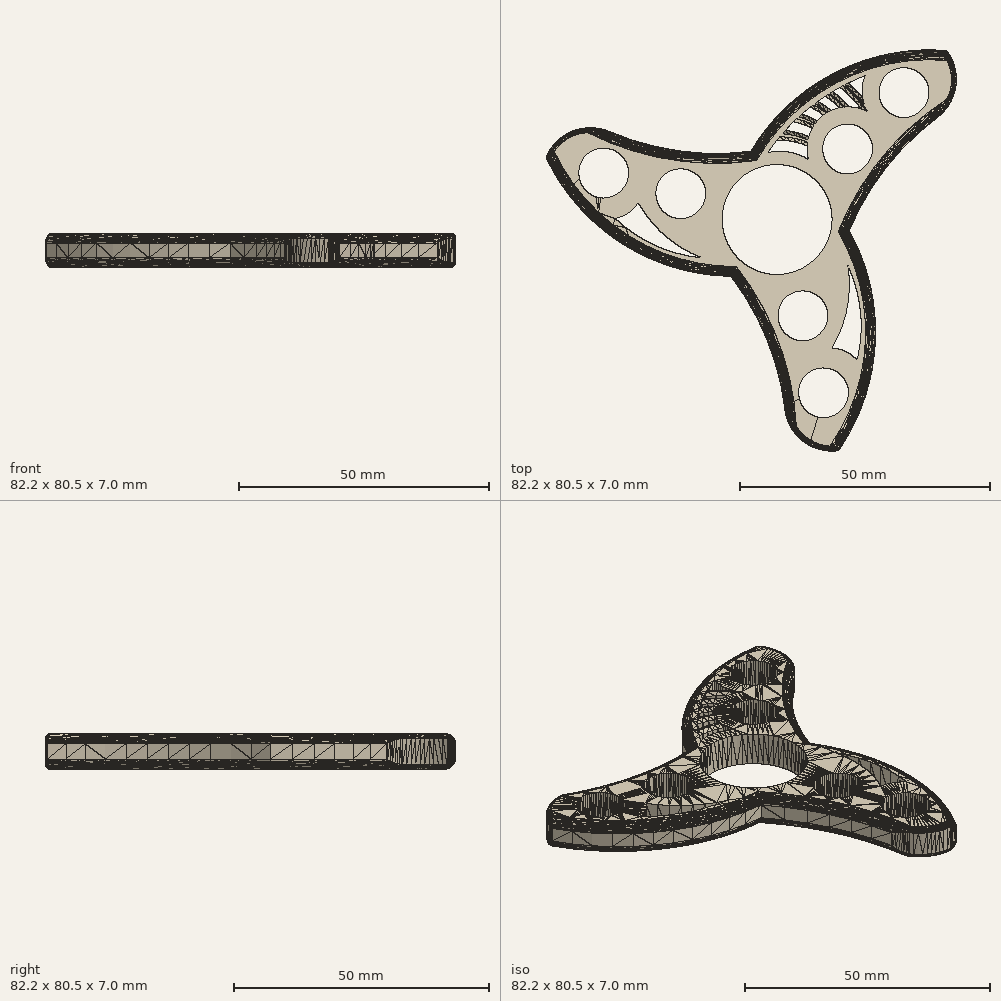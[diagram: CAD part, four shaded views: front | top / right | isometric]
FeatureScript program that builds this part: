
annotation { "Feature Type Name" : "Feature", "Feature Type Description" : "" }
export const myFeature = defineFeature(function(context is Context, id is Id, definition is map)
    precondition{}
    {
        {
            var Q0;
            Q0=qCreatedBy(makeId("Top.planeOp"),FACE);
            var sketch = newSketch(context, id + "F0", { "sketchPlane" : qUnion([Q0])});
            skCircle(sketch, "E0", {"center": v(0, 0) * mm, "radius": 11.03 * mm});
            skLineSegment(sketch, "E1", {"start": v(0, 0) * mm, "end": v(33.94, 33.94) * mm, "construction": true});
            skCircle(sketch, "E2", {"center": v(25.46, 25.46) * mm, "radius": 6.5 * mm, "construction": true});
            skCircle(sketch, "E3", {"center": v(14.14, 14.14) * mm, "radius": 6.5 * mm, "construction": true});
            skCircle(sketch, "E4", {"center": v(14.14, 14.14) * mm, "radius": 5 * mm});
            skCircle(sketch, "E5", {"center": v(25.46, 25.46) * mm, "radius": 5 * mm});
            skArc(sketch, "E6", {"start": v(33.94, 33.94) * mm, "mid": v(11.46, 29.38) * mm, "end": v(-5.27, 13.69) * mm});
            skArc(sketch, "E7", {"start": v(32.35, 20.51) * mm, "mid": v(21.9, 10.32) * mm, "end": v(14.49, -2.28) * mm});
            skArc(sketch, "E8", {"start": v(32.35, 20.51) * mm, "mid": v(35.92, 26.9) * mm, "end": v(33.94, 33.94) * mm});
            skArc(sketch, "E9.1.0", {"start": v(-33.94, 17.76) * mm, "mid": v(-41.25, 17.65) * mm, "end": v(-46.36, 12.42) * mm});
            skArc(sketch, "E9.1.1", {"start": v(-46.36, 12.42) * mm, "mid": v(-31.17, -4.76) * mm, "end": v(-9.22, -11.4) * mm});
            skArc(sketch, "E9.1.2", {"start": v(-32.47, 0.2) * mm, "mid": v(-29.84, 1.28) * mm, "end": v(-27.83, 3.32) * mm});
            skArc(sketch, "E9.1.3", {"start": v(-27.83, 3.32) * mm, "mid": v(-22.42, -3.3) * mm, "end": v(-15.06, -7.68) * mm});
            skArc(sketch, "E9.1.4", {"start": v(-32.47, 0.2) * mm, "mid": v(-24.43, -5.21) * mm, "end": v(-15.06, -7.68) * mm});
            skArc(sketch, "E9.1.5", {"start": v(-33.94, 17.76) * mm, "mid": v(-19.88, 13.8) * mm, "end": v(-5.27, 13.69) * mm});
            skCircle(sketch, "E9.1.6", {"center": v(-34.77, 9.32) * mm, "radius": 5 * mm});
            skCircle(sketch, "E9.1.7", {"center": v(-19.32, 5.18) * mm, "radius": 5 * mm});
            skCircle(sketch, "E9.1.8", {"center": v(-34.77, 9.32) * mm, "radius": 6.5 * mm, "construction": true});
            skCircle(sketch, "E9.1.9", {"center": v(-19.32, 5.18) * mm, "radius": 6.5 * mm, "construction": true});
            skArc(sketch, "E9.2.0", {"start": v(1.59, -38.28) * mm, "mid": v(5.34, -44.55) * mm, "end": v(12.42, -46.36) * mm});
            skArc(sketch, "E9.2.1", {"start": v(12.42, -46.36) * mm, "mid": v(19.7, -24.61) * mm, "end": v(14.49, -2.28) * mm});
            skArc(sketch, "E9.2.2", {"start": v(16.07, -28.22) * mm, "mid": v(13.8, -26.48) * mm, "end": v(11.04, -25.76) * mm});
            skArc(sketch, "E9.2.3", {"start": v(11.04, -25.76) * mm, "mid": v(14.07, -17.76) * mm, "end": v(14.18, -9.2) * mm});
            skArc(sketch, "E9.2.4", {"start": v(16.07, -28.22) * mm, "mid": v(16.73, -18.55) * mm, "end": v(14.18, -9.2) * mm});
            skArc(sketch, "E9.2.5", {"start": v(1.59, -38.28) * mm, "mid": v(-2.01, -24.12) * mm, "end": v(-9.22, -11.4) * mm});
            skCircle(sketch, "E9.2.6", {"center": v(9.32, -34.77) * mm, "radius": 5 * mm});
            skCircle(sketch, "E9.2.7", {"center": v(5.18, -19.32) * mm, "radius": 5 * mm});
            skCircle(sketch, "E9.2.8", {"center": v(9.32, -34.77) * mm, "radius": 6.5 * mm, "construction": true});
            skCircle(sketch, "E9.2.9", {"center": v(5.18, -19.32) * mm, "radius": 6.5 * mm, "construction": true});
            skPoint(sketch, "E10.orphan", {"position": v(-5.41, 13.45) * mm});
            skPoint(sketch, "E11.orphan", {"position": v(14.36, -2.04) * mm});
            skPoint(sketch, "E12.orphan", {"position": v(12.82, -6.77) * mm});
            skPoint(sketch, "E13.orphan", {"position": v(-12.27, -7.72) * mm});
            skPoint(sketch, "E14.orphan", {"position": v(-8.94, -11.41) * mm});
            skLineSegment(sketch, "E15", {"start": v(18.56, -32.6) * mm, "end": v(35.6, 25.32) * mm, "construction": true});
            skArc(sketch, "E16", {"start": v(17.66, 28.84) * mm, "mid": v(15.95, 28.13) * mm, "end": v(14.29, 27.35) * mm});
            skArc(sketch, "E17", {"start": v(6.3, 12.06) * mm, "mid": v(2.36, 13.55) * mm, "end": v(-1.83, 13.41) * mm});
            skArc(sketch, "E18", {"start": v(16.92, 22.19) * mm, "mid": v(15.73, 22.49) * mm, "end": v(14.51, 22.6) * mm});
            skArc(sketch, "E19", {"start": v(17.66, 28.84) * mm, "mid": v(17.1, 26.69) * mm, "end": v(17.14, 24.47) * mm});
            skArc(sketch, "E20.0.3.0", {"start": v(8.1, 19.77) * mm, "mid": v(6.61, 20.54) * mm, "end": v(5.06, 21.16) * mm});
            skLineSegment(sketch, "E20.direction1", {"start": v(0.3, 0.77) * mm, "end": v(25.3, 0.77) * mm, "construction": true});
            skLineSegment(sketch, "E20.direction2", {"start": v(0.3, 0.77) * mm, "end": v(0.3, 2.77) * mm, "construction": true});
            skArc(sketch, "E21", {"start": v(9.32, 20.93) * mm, "mid": v(8.06, 21.8) * mm, "end": v(6.7, 22.53) * mm});
            skArc(sketch, "E22", {"start": v(10.84, 21.84) * mm, "mid": v(9.57, 22.82) * mm, "end": v(8.22, 23.68) * mm});
            skArc(sketch, "E23", {"start": v(12.54, 22.42) * mm, "mid": v(11.18, 23.63) * mm, "end": v(9.72, 24.72) * mm});
            skPoint(sketch, "E23.startSnap0", {"position": v(13.15, 22.53) * mm});
            skArc(sketch, "E24", {"start": v(14.51, 22.6) * mm, "mid": v(12.93, 24.2) * mm, "end": v(11.2, 25.66) * mm});
            skArc(sketch, "E25", {"start": v(16.92, 22.19) * mm, "mid": v(14.9, 24.45) * mm, "end": v(12.67, 26.5) * mm});
            skArc(sketch, "E26", {"start": v(17.14, 24.47) * mm, "mid": v(15.76, 25.95) * mm, "end": v(14.29, 27.35) * mm});
            skArc(sketch, "E27.trimOffspring", {"start": v(-4.32, 15.2) * mm, "mid": v(-5.08, 14.93) * mm, "end": v(-5.82, 14.63) * mm});
            skArc(sketch, "E28.trimOffspring", {"start": v(6.05, 14.79) * mm, "mid": v(3.1, 15.66) * mm, "end": v(0.04, 15.92) * mm});
            skArc(sketch, "E29.trimOffspring", {"start": v(6.4, 16.64) * mm, "mid": v(4.1, 17.44) * mm, "end": v(1.7, 17.86) * mm});
            skArc(sketch, "E30.trimOffspring", {"start": v(7.1, 18.32) * mm, "mid": v(5.28, 19.08) * mm, "end": v(3.39, 19.6) * mm});
            skPoint(sketch, "E31.orphan", {"position": v(8.73, 19.36) * mm});
            skPoint(sketch, "E32.orphan", {"position": v(13.15, 21.8) * mm});
            skArc(sketch, "E33.trimOffspring", {"start": v(12.67, 26.5) * mm, "mid": v(11.94, 26.1) * mm, "end": v(11.2, 25.66) * mm});
            skArc(sketch, "E34.trimOffspring", {"start": v(9.72, 24.72) * mm, "mid": v(8.96, 24.21) * mm, "end": v(8.22, 23.68) * mm});
            skArc(sketch, "E35.trimOffspring", {"start": v(12.54, 22.42) * mm, "mid": v(11.68, 22.18) * mm, "end": v(10.84, 21.84) * mm});
            skArc(sketch, "E36.trimOffspring", {"start": v(6.7, 22.53) * mm, "mid": v(5.87, 21.85) * mm, "end": v(5.06, 21.16) * mm});
            skArc(sketch, "E37.trimOffspring", {"start": v(3.39, 19.6) * mm, "mid": v(2.53, 18.74) * mm, "end": v(1.7, 17.86) * mm});
            skArc(sketch, "E38.trimOffspring", {"start": v(7.1, 18.32) * mm, "mid": v(6.7, 17.5) * mm, "end": v(6.4, 16.64) * mm});
            skArc(sketch, "E39.trimOffspring", {"start": v(0.04, 15.92) * mm, "mid": v(-0.92, 14.68) * mm, "end": v(-1.83, 13.41) * mm});
            skArc(sketch, "E40.trimOffspring", {"start": v(6.05, 14.79) * mm, "mid": v(6.06, 13.41) * mm, "end": v(6.3, 12.06) * mm});
            skArc(sketch, "E41", {"start": v(9.32, 20.93) * mm, "mid": v(8.67, 20.4) * mm, "end": v(8.1, 19.77) * mm});
            skSolve(sketch);
        }
        {
            var Q0;
            Q0=makeQuery(id+"F0.imprint","IMPRINT",FACE,{"disambiguationData":[TD([[makeQuery(id+"F0.imprint","IMPRINT",EDGE,{"derivedFrom":sQuery(id+"F0.wireOp",EDGE,"E0")}),-1.0]])]});
            extrude(context, id + "F1", {"entities" : qUnion([Q0]), "depth" : 7 * mm});
        }
        {
            var Q0;
            Q0=makeQuery(id+"F1.opExtrude","CAP_EDGE",EDGE,{"disambiguationData":[OSD([sQuery(id+"F0.wireOp",EDGE,"E9.1.1")])],"isStart":false});
            var Q1;
            Q1=makeQuery(id+"F1.opExtrude","CAP_EDGE",EDGE,{"disambiguationData":[OSD([sQuery(id+"F0.wireOp",EDGE,"E9.2.5")])],"isStart":false});
            var Q2;
            Q2=makeQuery(id+"F1.opExtrude","CAP_EDGE",EDGE,{"disambiguationData":[OSD([sQuery(id+"F0.wireOp",EDGE,"E9.2.1")])],"isStart":false});
            var Q3;
            Q3=makeQuery(id+"F1.opExtrude","CAP_EDGE",EDGE,{"disambiguationData":[OSD([sQuery(id+"F0.wireOp",EDGE,"E7")])],"isStart":false});
            var Q4;
            Q4=makeQuery(id+"F1.opExtrude","CAP_EDGE",EDGE,{"disambiguationData":[OSD([sQuery(id+"F0.wireOp",EDGE,"E6")])],"isStart":false});
            var Q5;
            Q5=makeQuery(id+"F1.opExtrude","CAP_EDGE",EDGE,{"disambiguationData":[OSD([sQuery(id+"F0.wireOp",EDGE,"E9.1.5")])],"isStart":false});
            var Q6;
            Q6=makeQuery(id+"F1.opExtrude","CAP_EDGE",EDGE,{"disambiguationData":[OSD([sQuery(id+"F0.wireOp",EDGE,"E6")])],"isStart":true});
            var Q7;
            Q7=makeQuery(id+"F1.opExtrude","CAP_EDGE",EDGE,{"disambiguationData":[OSD([sQuery(id+"F0.wireOp",EDGE,"E9.1.5")])],"isStart":true});
            var Q8;
            Q8=makeQuery(id+"F1.opExtrude","CAP_EDGE",EDGE,{"disambiguationData":[OSD([sQuery(id+"F0.wireOp",EDGE,"E7")])],"isStart":true});
            var Q9;
            Q9=makeQuery(id+"F1.opExtrude","CAP_EDGE",EDGE,{"disambiguationData":[OSD([sQuery(id+"F0.wireOp",EDGE,"E9.2.1")])],"isStart":true});
            var Q10;
            Q10=makeQuery(id+"F1.opExtrude","CAP_EDGE",EDGE,{"disambiguationData":[OSD([sQuery(id+"F0.wireOp",EDGE,"E9.2.5")])],"isStart":true});
            var Q11;
            Q11=makeQuery(id+"F1.opExtrude","CAP_EDGE",EDGE,{"disambiguationData":[OSD([sQuery(id+"F0.wireOp",EDGE,"E9.1.1")])],"isStart":true});
            fillet(context, id + "F2", {"entities" : qUnion([Q0, Q1, Q2, Q3, Q4, Q5, Q6, Q7, Q8, Q9, Q10, Q11]), "radius" : 2 * mm, "tangentPropagation" : true, "allowEdgeOverflow" : false});
        }
        {
            var Q0;
            Q0=makeQuery(id+"F1.opExtrude","CAP_EDGE",EDGE,{"disambiguationData":[OSD([sQuery(id+"F0.wireOp",EDGE,"E9.1.0")])],"isStart":false});
            var Q1;
            Q1=makeQuery(id+"F1.opExtrude","CAP_EDGE",EDGE,{"disambiguationData":[OSD([sQuery(id+"F0.wireOp",EDGE,"E9.2.0")])],"isStart":false});
            var Q2;
            Q2=makeQuery(id+"F1.opExtrude","CAP_EDGE",EDGE,{"disambiguationData":[OSD([sQuery(id+"F0.wireOp",EDGE,"E8")])],"isStart":false});
            var Q3;
            Q3=makeQuery(id+"F1.opExtrude","CAP_EDGE",EDGE,{"disambiguationData":[OSD([sQuery(id+"F0.wireOp",EDGE,"E9.2.0")])],"isStart":true});
            var Q4;
            Q4=makeQuery(id+"F1.opExtrude","CAP_EDGE",EDGE,{"disambiguationData":[OSD([sQuery(id+"F0.wireOp",EDGE,"E9.1.0")])],"isStart":true});
            var Q5;
            Q5=makeQuery(id+"F1.opExtrude","CAP_EDGE",EDGE,{"disambiguationData":[OSD([sQuery(id+"F0.wireOp",EDGE,"E8")])],"isStart":true});
            fillet(context, id + "F3", {"entities" : qUnion([Q0, Q1, Q2, Q3, Q4, Q5]), "radius" : 1 * mm, "tangentPropagation" : true, "allowEdgeOverflow" : false});
        }
        {
            var Q0;
            Q0=makeQuery(id+"F1.opExtrude","CAP_EDGE",EDGE,{"disambiguationData":[OSD([sQuery(id+"F0.wireOp",EDGE,"E28.trimOffspring")])],"isStart":false});
            var Q1;
            Q1=makeQuery(id+"F1.opExtrude","CAP_EDGE",EDGE,{"disambiguationData":[OSD([sQuery(id+"F0.wireOp",EDGE,"E29.trimOffspring")])],"isStart":false});
            var Q2;
            Q2=makeQuery(id+"F1.opExtrude","CAP_EDGE",EDGE,{"disambiguationData":[OSD([sQuery(id+"F0.wireOp",EDGE,"E20.0.3.0")])],"isStart":false});
            var Q3;
            Q3=makeQuery(id+"F1.opExtrude","CAP_EDGE",EDGE,{"disambiguationData":[OSD([sQuery(id+"F0.wireOp",EDGE,"E21")])],"isStart":false});
            var Q4;
            Q4=makeQuery(id+"F1.opExtrude","CAP_EDGE",EDGE,{"disambiguationData":[OSD([sQuery(id+"F0.wireOp",EDGE,"E22")])],"isStart":false});
            var Q5;
            Q5=makeQuery(id+"F1.opExtrude","CAP_EDGE",EDGE,{"disambiguationData":[OSD([sQuery(id+"F0.wireOp",EDGE,"E23")])],"isStart":false});
            var Q6;
            Q6=makeQuery(id+"F1.opExtrude","CAP_EDGE",EDGE,{"disambiguationData":[OSD([sQuery(id+"F0.wireOp",EDGE,"E24")])],"isStart":false});
            var Q7;
            Q7=makeQuery(id+"F1.opExtrude","CAP_EDGE",EDGE,{"disambiguationData":[OSD([sQuery(id+"F0.wireOp",EDGE,"E25")])],"isStart":false});
            var Q8;
            Q8=makeQuery(id+"F1.opExtrude","CAP_EDGE",EDGE,{"disambiguationData":[OSD([sQuery(id+"F0.wireOp",EDGE,"E26")])],"isStart":false});
            var Q9;
            Q9=makeQuery(id+"F1.opExtrude","CAP_EDGE",EDGE,{"disambiguationData":[OSD([sQuery(id+"F0.wireOp",EDGE,"E30.trimOffspring")])],"isStart":false});
            var Q10;
            Q10=makeQuery(id+"F1.opExtrude","CAP_EDGE",EDGE,{"disambiguationData":[OSD([sQuery(id+"F0.wireOp",EDGE,"E28.trimOffspring")])],"isStart":true});
            var Q11;
            Q11=makeQuery(id+"F1.opExtrude","CAP_EDGE",EDGE,{"disambiguationData":[OSD([sQuery(id+"F0.wireOp",EDGE,"E29.trimOffspring")])],"isStart":true});
            var Q12;
            Q12=makeQuery(id+"F1.opExtrude","CAP_EDGE",EDGE,{"disambiguationData":[OSD([sQuery(id+"F0.wireOp",EDGE,"E30.trimOffspring")])],"isStart":true});
            var Q13;
            Q13=makeQuery(id+"F1.opExtrude","CAP_EDGE",EDGE,{"disambiguationData":[OSD([sQuery(id+"F0.wireOp",EDGE,"E20.0.3.0")])],"isStart":true});
            var Q14;
            Q14=makeQuery(id+"F1.opExtrude","CAP_EDGE",EDGE,{"disambiguationData":[OSD([sQuery(id+"F0.wireOp",EDGE,"E21")])],"isStart":true});
            var Q15;
            Q15=makeQuery(id+"F1.opExtrude","CAP_EDGE",EDGE,{"disambiguationData":[OSD([sQuery(id+"F0.wireOp",EDGE,"E22")])],"isStart":true});
            var Q16;
            Q16=makeQuery(id+"F1.opExtrude","CAP_EDGE",EDGE,{"disambiguationData":[OSD([sQuery(id+"F0.wireOp",EDGE,"E23")])],"isStart":true});
            var Q17;
            Q17=makeQuery(id+"F1.opExtrude","CAP_EDGE",EDGE,{"disambiguationData":[OSD([sQuery(id+"F0.wireOp",EDGE,"E24")])],"isStart":true});
            var Q18;
            Q18=makeQuery(id+"F1.opExtrude","CAP_EDGE",EDGE,{"disambiguationData":[OSD([sQuery(id+"F0.wireOp",EDGE,"E25")])],"isStart":true});
            var Q19;
            Q19=makeQuery(id+"F1.opExtrude","CAP_EDGE",EDGE,{"disambiguationData":[OSD([sQuery(id+"F0.wireOp",EDGE,"E26")])],"isStart":true});
            chamfer(context, id + "F4", {"entities" : qUnion([Q0, Q1, Q2, Q3, Q4, Q5, Q6, Q7, Q8, Q9, Q10, Q11, Q12, Q13, Q14, Q15, Q16, Q17, Q18, Q19]), "width" : .7 * mm, "tangentPropagation" : true});
        }
    });
